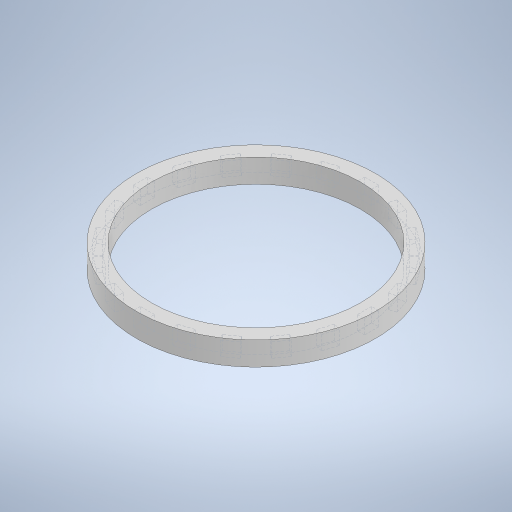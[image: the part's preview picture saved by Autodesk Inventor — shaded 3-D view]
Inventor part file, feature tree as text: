
AUTODESK INVENTOR PART (.ipt)
format: ipt  version: 2023 (Build 270158000, 158)  size: 357,376 bytes
history: native  units: mm
features: extrude x2, sketch x2
ambient origin geometry x8: Origin, YZ Plane, XZ Plane, XY Plane, X Axis, Y Axis, Z Axis, Center Point
bodies: Solid1 (feature_tree)
feature tree (4):
  extrude  "Extrusion1"  Depth=101.6mm
  extrude  "Extrusion2"  Depth=3.0mm
  sketch  "Sketch1"  dims[d0=88.9mm d1=101.6mm]
  sketch  "Sketch2"  dims[d2=10.0mm d3=0.0mm d4=3.0mm d5=6.0mm d6=200.0mm d8=360.0deg d10=6.0mm d11=0.0mm]
